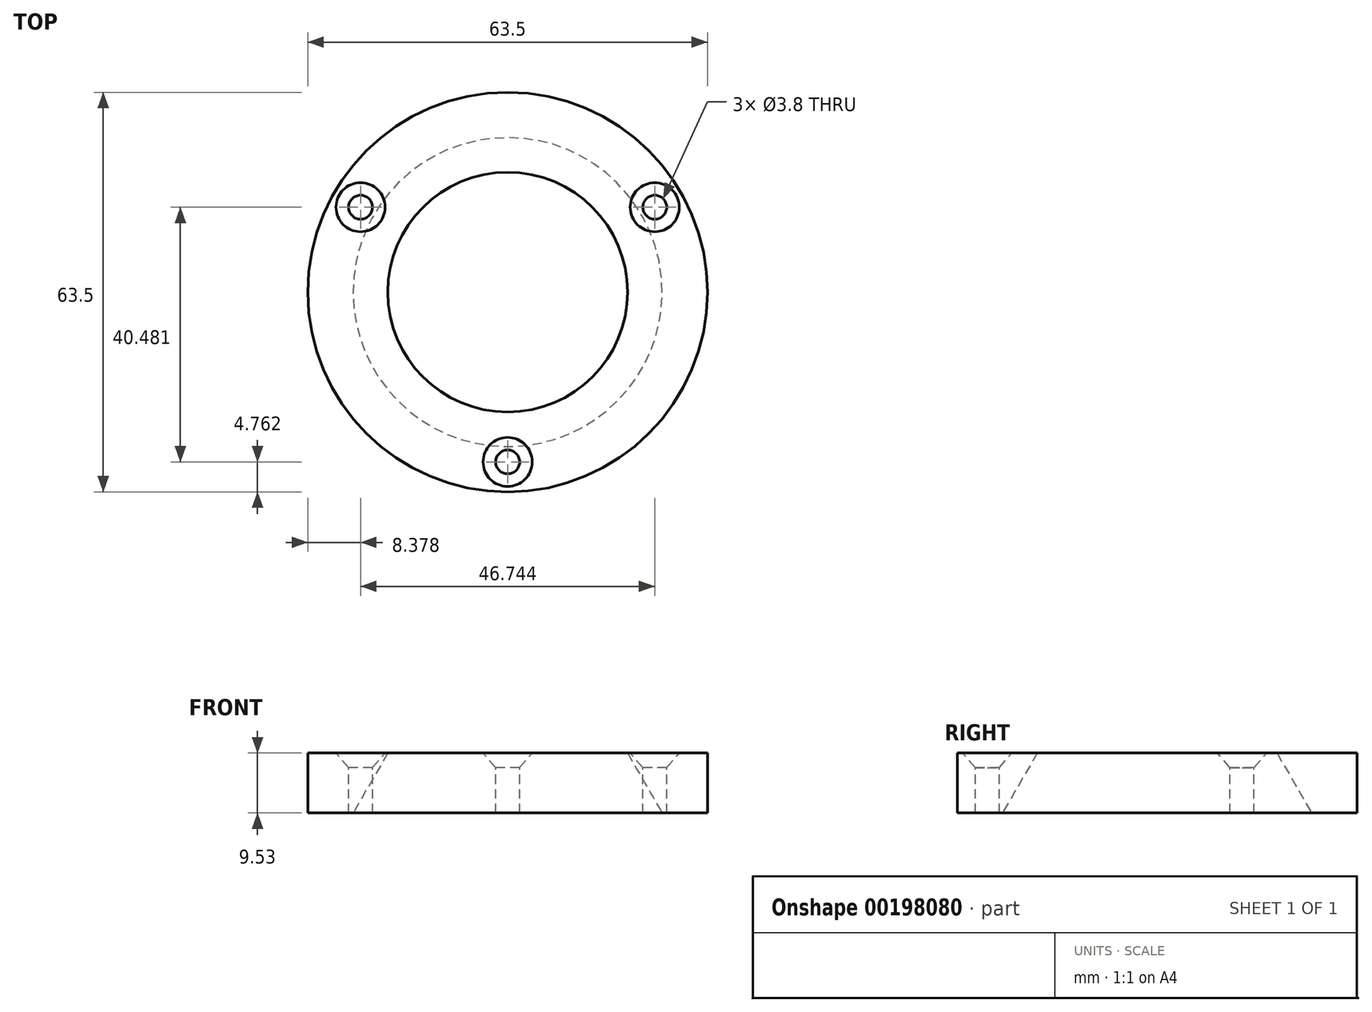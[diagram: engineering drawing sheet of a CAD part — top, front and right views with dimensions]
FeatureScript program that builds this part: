
annotation { "Feature Type Name" : "Feature", "Feature Type Description" : "" }
export const myFeature = defineFeature(function(context is Context, id is Id, definition is map)
    precondition{}
    {
        {
            var Q0;
            Q0=qCreatedBy(makeId("Top.planeOp"),FACE);
            var sketch = newSketch(context, id + "F0", { "sketchPlane" : qUnion([Q0])});
            skCircle(sketch, "E0", {"center": v(0, 0) * mm, "radius": 31.75 * mm});
            skSolve(sketch);
        }
        {
            var Q0;
            Q0 = qSketchRegion(id + "F0", true);
            extrude(context, id + "F1", {"entities" : qUnion([Q0]), "depth" : 9.52 * mm});
        }
        {
            var Q0;
            Q0=makeQuery(id+"F1.opExtrude","CAP_FACE",FACE,{"disambiguationData":[OSD([sQuery(id+"F0.wireOp",EDGE,"E0")])],"isStart":false});
            var sketch = newSketch(context, id + "F2", { "sketchPlane" : qUnion([Q0])});
            skCircle(sketch, "E1", {"center": v(0, 0) * mm, "radius": 19.05 * mm});
            skSolve(sketch);
        }
        {
            var Q0;
            Q0 = qSketchRegion(id + "F2", true);
            extrude(context, id + "F3", {"entities" : qUnion([Q0]), "operationType" : NewBodyOperationType.REMOVE, "oppositeDirection" : true, "depth" : 25.4 * mm, "hasDraft" : true, "draftAngle" : 30 * degree});
        }
        {
            var Q0;
            Q0=makeQuery(id+"F1.opExtrude","CAP_FACE",FACE,{"disambiguationData":[OSD([sQuery(id+"F0.wireOp",EDGE,"E0")])],"isStart":false});
            var sketch = newSketch(context, id + "F4", { "sketchPlane" : qUnion([Q0])});
            skCircle(sketch, "E2.0", {"center": v(0, 0) * mm, "radius": 26.99 * mm, "construction": true});
            skPoint(sketch, "E3", {"position": v(0, -26.99) * mm});
            skPoint(sketch, "E4.1.0", {"position": v(23.37, 13.5) * mm});
            skPoint(sketch, "E4.2.0", {"position": v(-23.37, 13.5) * mm});
            skSolve(sketch);
        }
        {
            var Q0;
            Q0=sQuery(id+"F4.wireOp",VERTEX,"E4.2.0");
            var Q1;
            Q1=sQuery(id+"F4.wireOp",VERTEX,"E4.1.0");
            var Q2;
            Q2=sQuery(id+"F4.wireOp",VERTEX,"E3");
            var Q3;
            Q3=makeQuery(id+"F1.opExtrude","SWEPT_BODY",BODY,{"disambiguationData":[OSD([sQuery(id+"F0.wireOp",EDGE,"E0")])]});
            hole(context, id + "F5", {"style" : HoleStyle.C_SINK, "endStyle" : HoleEndStyle.THROUGH, "standardTappedOrClearance" : lookupTablePath({ "standard" : "ANSI", "fit" : "Normal (ASME)", "size" : "#6", "type" : "Clearance" }), "standardBlindInLast" : lookupTablePath({ "fit" : "Free", "standard" : "ANSI", "size" : "#6", "type" : "Clearance" }), "holeDiameter" : 3.8 * mm, "cSinkDiameter" : 7.8 * mm, "cSinkAngle" : 82 * degree, "startFromSketch" : true, "locations" : qUnion([Q0, Q1, Q2]), "scope" : qUnion([Q3]), "isTappedThrough" : true});
        }
    });
